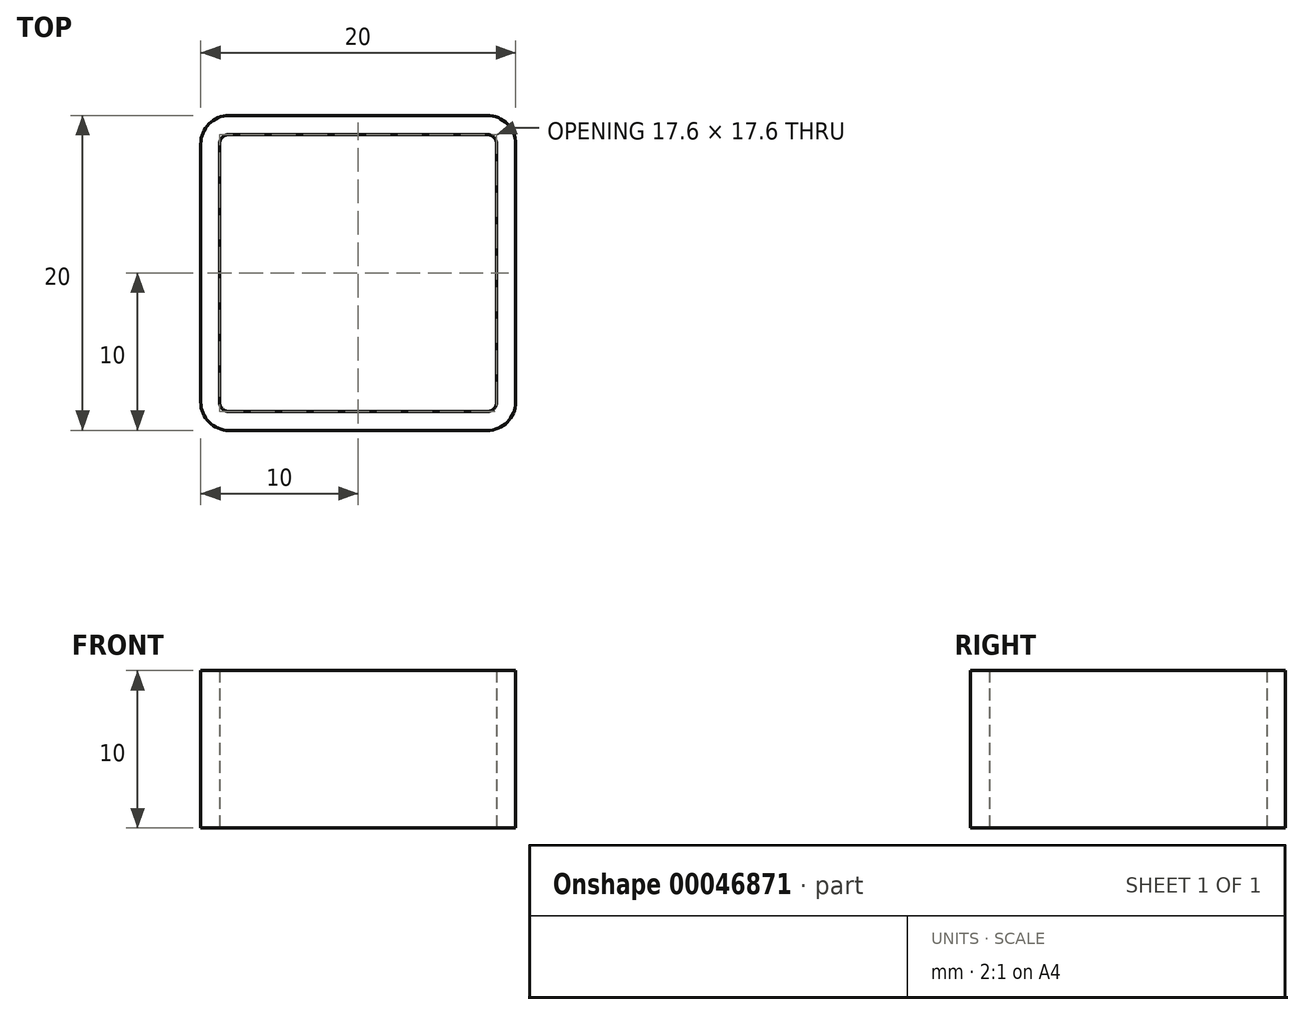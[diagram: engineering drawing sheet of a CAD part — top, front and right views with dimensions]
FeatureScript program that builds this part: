
annotation { "Feature Type Name" : "Feature", "Feature Type Description" : "" }
export const myFeature = defineFeature(function(context is Context, id is Id, definition is map)
    precondition{}
    {
        {
            var Q0;
            Q0=qCreatedBy(makeId("Top.planeOp"),FACE);
            var sketch = newSketch(context, id + "F0", { "sketchPlane" : qUnion([Q0])});
            skLineSegment(sketch, "E0.rect.bottom", {"start": v(10, 10) * mm, "end": v(-10, 10) * mm});
            skLineSegment(sketch, "E0.rect.top", {"start": v(10, -10) * mm, "end": v(-10, -10) * mm});
            skLineSegment(sketch, "E0.rect.left", {"start": v(10, 10) * mm, "end": v(10, -10) * mm});
            skLineSegment(sketch, "E0.rect.right", {"start": v(-10, 10) * mm, "end": v(-10, -10) * mm});
            skPoint(sketch, "E0.rect.middle", {"position": v(0, 0) * mm});
            skLineSegment(sketch, "E1.rect.bottom", {"start": v(8.8, 8.8) * mm, "end": v(-8.8, 8.8) * mm});
            skLineSegment(sketch, "E1.rect.top", {"start": v(8.8, -8.8) * mm, "end": v(-8.8, -8.8) * mm});
            skLineSegment(sketch, "E1.rect.left", {"start": v(8.8, 8.8) * mm, "end": v(8.8, -8.8) * mm});
            skLineSegment(sketch, "E1.rect.right", {"start": v(-8.8, 8.8) * mm, "end": v(-8.8, -8.8) * mm});
            skSolve(sketch);
        }
        {
            var Q0;
            Q0=makeQuery(id+"F0.imprint","IMPRINT",FACE,{"disambiguationData":[TD([[makeQuery(id+"F0.imprint","IMPRINT",EDGE,{"derivedFrom":sQuery(id+"F0.wireOp",EDGE,"E0.rect.bottom")}),1.0]])]});
            extrude(context, id + "F1", {"entities" : qUnion([Q0]), "depth" : 10 * mm});
        }
        {
            var Q0;
            Q0=makeQuery(id+"F1.opExtrude","SWEPT_EDGE",EDGE,{"disambiguationData":[OSD([sQuery(id+"F0.wireOp",EDGE,"E0.rect.top"),sQuery(id+"F0.wireOp",EDGE,"E0.rect.left")])]});
            fillet(context, id + "F2", {"entities" : qUnion([Q0]), "radius" : 1.8 * mm, "tangentPropagation" : true, "allowEdgeOverflow" : false});
        }
        {
            var Q0;
            Q0=makeQuery(id+"F1.opExtrude","SWEPT_EDGE",EDGE,{"disambiguationData":[OSD([sQuery(id+"F0.wireOp",EDGE,"E0.rect.bottom"),sQuery(id+"F0.wireOp",EDGE,"E0.rect.left")])]});
            fillet(context, id + "F3", {"entities" : qUnion([Q0]), "radius" : 1.8 * mm, "tangentPropagation" : true, "allowEdgeOverflow" : false});
        }
        {
            var Q0;
            Q0=makeQuery(id+"F1.opExtrude","SWEPT_EDGE",EDGE,{"disambiguationData":[OSD([sQuery(id+"F0.wireOp",EDGE,"E0.rect.bottom"),sQuery(id+"F0.wireOp",EDGE,"E0.rect.right")])]});
            fillet(context, id + "F4", {"entities" : qUnion([Q0]), "radius" : 1.8 * mm, "tangentPropagation" : true, "allowEdgeOverflow" : false});
        }
        {
            var Q0;
            Q0=makeQuery(id+"F1.opExtrude","SWEPT_EDGE",EDGE,{"disambiguationData":[OSD([sQuery(id+"F0.wireOp",EDGE,"E0.rect.top"),sQuery(id+"F0.wireOp",EDGE,"E0.rect.right")])]});
            fillet(context, id + "F5", {"entities" : qUnion([Q0]), "radius" : 1.8 * mm, "tangentPropagation" : true, "allowEdgeOverflow" : false});
        }
        {
            var Q0;
            Q0=makeQuery(id+"F1.opExtrude","SWEPT_EDGE",EDGE,{"disambiguationData":[OSD([sQuery(id+"F0.wireOp",EDGE,"E1.rect.bottom"),sQuery(id+"F0.wireOp",EDGE,"E1.rect.right")])]});
            fillet(context, id + "F6", {"entities" : qUnion([Q0]), "radius" : 0.6 * mm, "tangentPropagation" : true, "allowEdgeOverflow" : false});
        }
        {
            var Q0;
            Q0=makeQuery(id+"F1.opExtrude","SWEPT_EDGE",EDGE,{"disambiguationData":[OSD([sQuery(id+"F0.wireOp",EDGE,"E1.rect.top"),sQuery(id+"F0.wireOp",EDGE,"E1.rect.right")])]});
            fillet(context, id + "F7", {"entities" : qUnion([Q0]), "radius" : 0.6 * mm, "tangentPropagation" : true, "allowEdgeOverflow" : false});
        }
        {
            var Q0;
            Q0=makeQuery(id+"F1.opExtrude","SWEPT_EDGE",EDGE,{"disambiguationData":[OSD([sQuery(id+"F0.wireOp",EDGE,"E1.rect.top"),sQuery(id+"F0.wireOp",EDGE,"E1.rect.left")])]});
            fillet(context, id + "F8", {"entities" : qUnion([Q0]), "radius" : 0.6 * mm, "tangentPropagation" : true, "allowEdgeOverflow" : false});
        }
        {
            var Q0;
            Q0=makeQuery(id+"F1.opExtrude","SWEPT_EDGE",EDGE,{"disambiguationData":[OSD([sQuery(id+"F0.wireOp",EDGE,"E1.rect.bottom"),sQuery(id+"F0.wireOp",EDGE,"E1.rect.left")])]});
            fillet(context, id + "F9", {"entities" : qUnion([Q0]), "radius" : 0.6 * mm, "tangentPropagation" : true, "allowEdgeOverflow" : false});
        }
    });
